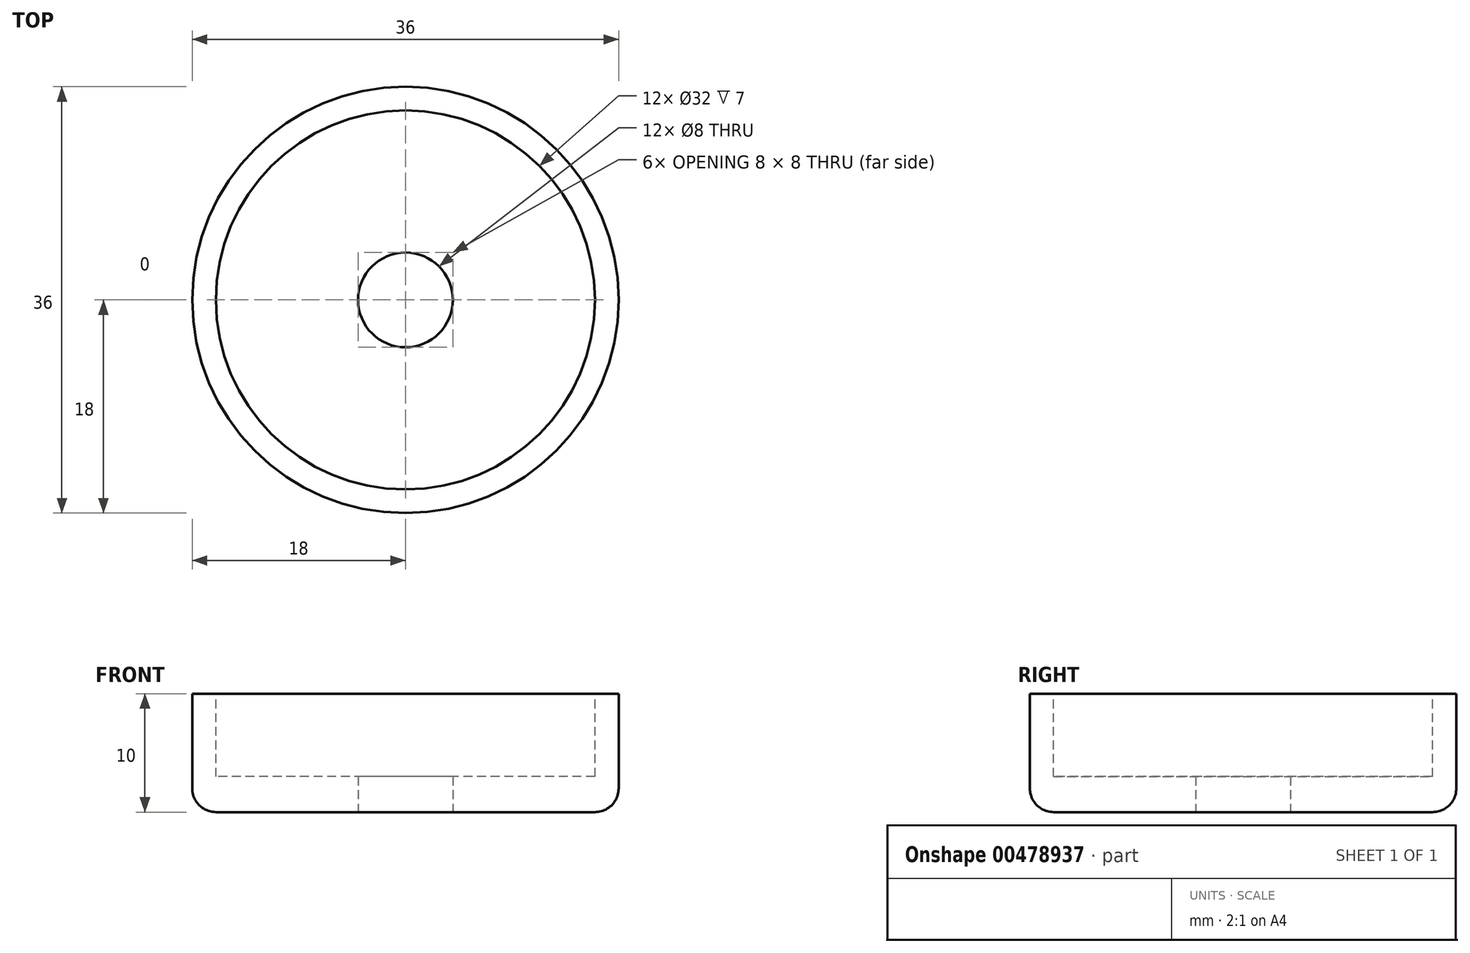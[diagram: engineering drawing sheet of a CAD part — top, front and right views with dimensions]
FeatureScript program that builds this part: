
annotation { "Feature Type Name" : "Feature", "Feature Type Description" : "" }
export const myFeature = defineFeature(function(context is Context, id is Id, definition is map)
    precondition{}
    {
        {
            var Q0;
            Q0=qCreatedBy(makeId("Top.planeOp"),FACE);
            var sketch = newSketch(context, id + "F0", { "sketchPlane" : qUnion([Q0])});
            skCircle(sketch, "E0", {"center": v(0, 0) * mm, "radius": 18 * mm});
            skSolve(sketch);
        }
        {
            var Q0;
            Q0=qSketchRegion(id+"F0",true);
            extrude(context, id + "F1", {"entities" : qUnion([Q0]), "depth" : 10 * mm});
        }
        {
            var Q0;
            Q0=makeQuery(id+"F1.opExtrude","CAP_FACE",FACE,{"disambiguationData":[OSD([sQuery(id+"F0.wireOp",EDGE,"E0")])],"isStart":false});
            var sketch = newSketch(context, id + "F2", { "sketchPlane" : qUnion([Q0])});
            skCircle(sketch, "E1", {"center": v(0, 0) * mm, "radius": 16 * mm});
            skSolve(sketch);
        }
        {
            var Q0;
            Q0=qSketchRegion(id+"F2",true);
            extrude(context, id + "F3", {"entities" : qUnion([Q0]), "operationType" : NewBodyOperationType.REMOVE, "oppositeDirection" : true, "depth" : 7 * mm});
        }
        {
            var Q0;
            Q0=makeQuery(id+"F1.opExtrude","CAP_FACE",FACE,{"disambiguationData":[OSD([sQuery(id+"F0.wireOp",EDGE,"E0")])],"isStart":true});
            var sketch = newSketch(context, id + "F4", { "sketchPlane" : qUnion([Q0])});
            skCircle(sketch, "E2", {"center": v(0, 0) * mm, "radius": 4 * mm});
            skSolve(sketch);
        }
        {
            var Q0;
            Q0=qSketchRegion(id+"F4",true);
            extrude(context, id + "F5", {"entities" : qUnion([Q0]), "operationType" : NewBodyOperationType.REMOVE, "oppositeDirection" : true, "depth" : 25 * mm});
        }
        {
            var Q0;
            Q0=makeQuery(id+"F1.opExtrude","CAP_EDGE",EDGE,{"disambiguationData":[OSD([sQuery(id+"F0.wireOp",EDGE,"E0")])],"isStart":true});
            fillet(context, id + "F6", {"entities" : qUnion([Q0]), "radius" : 2 * mm, "tangentPropagation" : true, "allowEdgeOverflow" : false});
        }
    });
